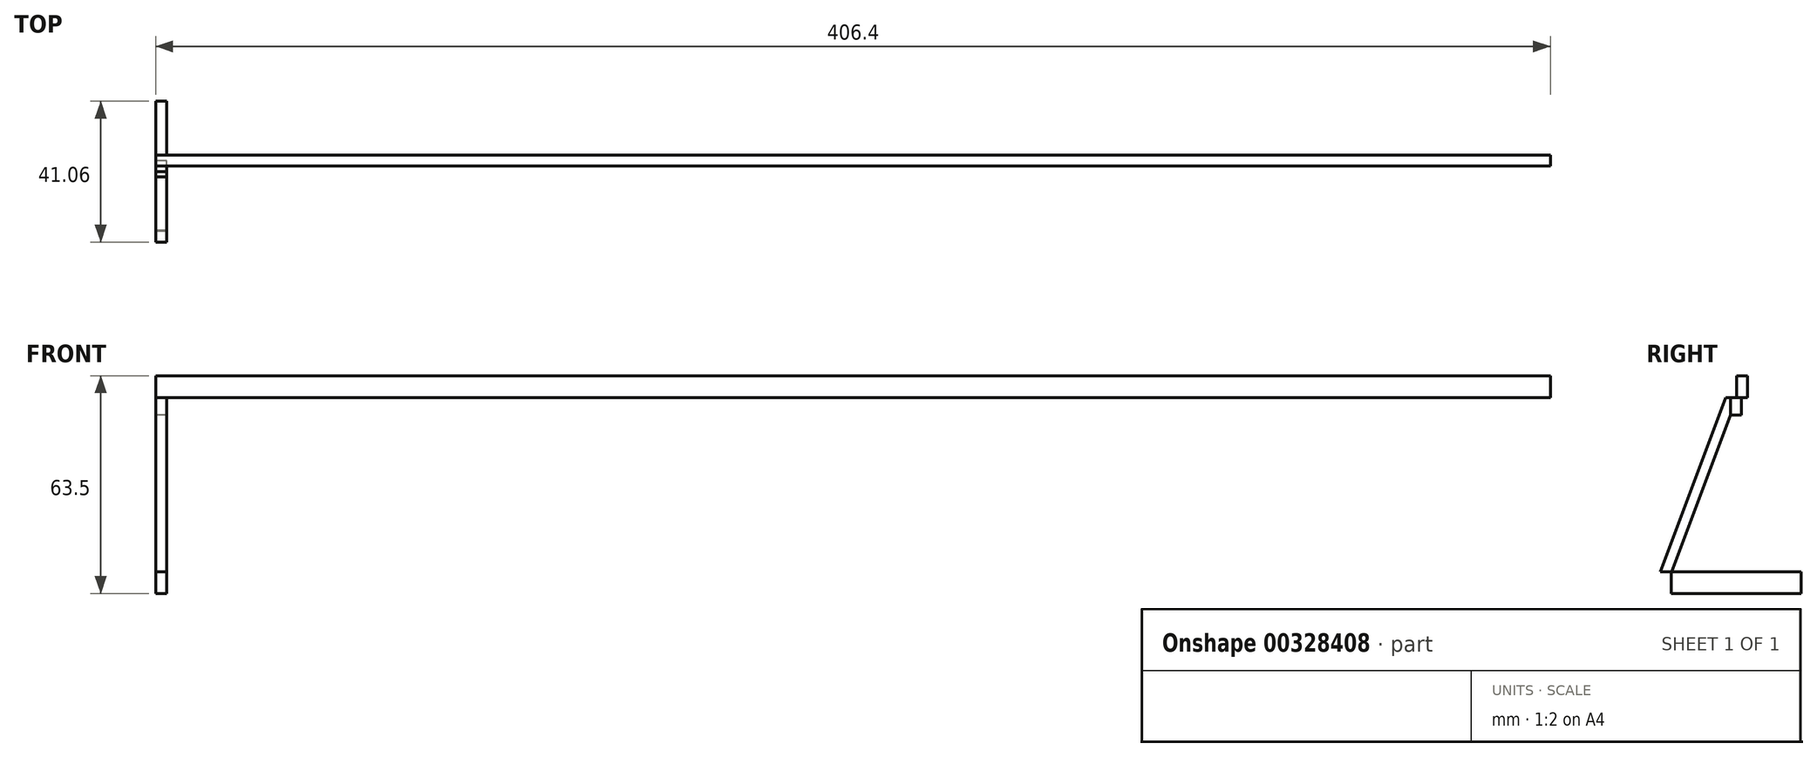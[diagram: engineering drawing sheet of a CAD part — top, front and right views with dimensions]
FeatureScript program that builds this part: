
annotation { "Feature Type Name" : "Feature", "Feature Type Description" : "" }
export const myFeature = defineFeature(function(context is Context, id is Id, definition is map)
    precondition{}
    {
        {
            var Q0;
            Q0=qCreatedBy(makeId("Right.planeOp"),FACE);
            var sketch = newSketch(context, id + "F0", { "sketchPlane" : qUnion([Q0])});
            skLineSegment(sketch, "E0", {"start": v(0, 0) * mm, "end": v(37.88, 0) * mm});
            skLineSegment(sketch, "E1", {"start": v(37.88, 0) * mm, "end": v(41.06, 0) * mm});
            skLineSegment(sketch, "E2", {"start": v(0, 0) * mm, "end": v(-3.17, 0) * mm});
            skLineSegment(sketch, "E3", {"start": v(41.06, 0) * mm, "end": v(41.06, 6.35) * mm});
            skLineSegment(sketch, "E4", {"start": v(-3.17, 0) * mm, "end": v(-3.17, 6.35) * mm});
            skLineSegment(sketch, "E5", {"start": v(0, 0) * mm, "end": v(0, 6.35) * mm});
            skLineSegment(sketch, "E6", {"start": v(37.88, 0) * mm, "end": v(37.88, 6.35) * mm});
            skLineSegment(sketch, "E7", {"start": v(-3.17, 6.35) * mm, "end": v(0, 6.35) * mm});
            skLineSegment(sketch, "E8", {"start": v(37.88, 6.35) * mm, "end": v(41.06, 6.35) * mm});
            skLineSegment(sketch, "E9", {"start": v(18.94, 0) * mm, "end": v(18.94, 52.05) * mm, "construction": true});
            skLineSegment(sketch, "E10", {"start": v(15.88, 57.15) * mm, "end": v(22.23, 57.15) * mm});
            skLineSegment(sketch, "E11", {"start": v(22.23, 57.15) * mm, "end": v(22.23, 63.5) * mm});
            skLineSegment(sketch, "E12", {"start": v(15.88, 57.15) * mm, "end": v(15.88, 63.5) * mm});
            skLineSegment(sketch, "E13", {"start": v(15.88, 63.5) * mm, "end": v(22.23, 63.5) * mm});
            skLineSegment(sketch, "E14", {"start": v(19.05, 57.15) * mm, "end": v(19.05, 63.5) * mm});
            skLineSegment(sketch, "E15", {"start": v(-3.17, 6.35) * mm, "end": v(15.88, 57.15) * mm});
            skLineSegment(sketch, "E16", {"start": v(22.23, 57.15) * mm, "end": v(41.06, 6.35) * mm});
            skLineSegment(sketch, "E17", {"start": v(0, 6.35) * mm, "end": v(37.88, 6.35) * mm});
            skLineSegment(sketch, "E18.trimOffspring", {"start": v(0.22, 6.35) * mm, "end": v(17.35, 52.05) * mm});
            skLineSegment(sketch, "E19", {"start": v(20.53, 52.05) * mm, "end": v(37.47, 6.35) * mm});
            skLineSegment(sketch, "E20", {"start": v(18.94, 6.35) * mm, "end": v(17.35, 6.35) * mm});
            skLineSegment(sketch, "E21", {"start": v(18.94, 6.35) * mm, "end": v(20.53, 6.35) * mm});
            skLineSegment(sketch, "E22", {"start": v(17.35, 6.35) * mm, "end": v(17.35, 52.05) * mm});
            skLineSegment(sketch, "E23", {"start": v(17.35, 52.05) * mm, "end": v(20.53, 52.05) * mm});
            skLineSegment(sketch, "E24", {"start": v(20.53, 52.05) * mm, "end": v(20.53, 6.35) * mm});
            skLineSegment(sketch, "E25", {"start": v(17.35, 52.05) * mm, "end": v(17.35, 57.15) * mm});
            skLineSegment(sketch, "E26", {"start": v(20.53, 52.05) * mm, "end": v(20.53, 57.15) * mm});
            skSolve(sketch);
        }
        {
            var Q0;
            {var subQ0=sQuery(id+"F0.wireOp",EDGE,"E11");Q0=makeQuery(id+"F0.imprint","IMPRINT",FACE,{"disambiguationData":[TD([[makeQuery(id+"F0.imprint","IMPRINT",EDGE,{"derivedFrom":subQ0}),1.0]])]});}
            extrude(context, id + "F1", {"entities" : qUnion([Q0]), "depth" : 406.4 * mm});
        }
        {
            var Q0;
            Q0=makeQuery(id+"F0.imprint","IMPRINT",FACE,{"disambiguationData":[TD([[makeQuery(id+"F0.imprint","IMPRINT",EDGE,{"derivedFrom":sQuery(id+"F0.wireOp",EDGE,"E7")}),1.0]])]});
            extrude(context, id + "F2", {"entities" : qUnion([Q0]), "depth" : 3.17 * mm});
        }
        {
            var Q0;
            Q0=makeQuery(id+"F0.imprint","IMPRINT",FACE,{"disambiguationData":[TD([[makeQuery(id+"F0.imprint","IMPRINT",EDGE,{"derivedFrom":sQuery(id+"F0.wireOp",EDGE,"E0")}),1.0]])]});
            extrude(context, id + "F3", {"entities" : qUnion([Q0]), "depth" : 3.17 * mm});
        }
        {
            var Q0;
            Q0=makeQuery(id+"F0.imprint","IMPRINT",FACE,{"disambiguationData":[TD([[makeQuery(id+"F0.imprint","IMPRINT",EDGE,{"derivedFrom":sQuery(id+"F0.wireOp",EDGE,"E20")}),-1.0]])]});
            var Q1;
            {var subQ0=sQuery(id+"F0.wireOp",EDGE,"pGliAPCi-6uMI-fG8I-oafq-WGV2nKLFa70K");Q1=makeQuery(id+"F0.imprint","IMPRINT",FACE,{"disambiguationData":[TD([[makeQuery(id+"F0.imprint","IMPRINT",EDGE,{"derivedFrom":subQ0}),1.0]])]});}
            var Q2;
            {var subQ3=sQuery(id+"F0.wireOp",EDGE,"E23");Q2=makeQuery(id+"F0.imprint","IMPRINT",FACE,{"disambiguationData":[TD([[makeQuery(id+"F0.imprint","IMPRINT",EDGE,{"derivedFrom":subQ3}),1.0]])]});}
            var Q3;
            {var subQ0=sQuery(id+"F0.wireOp",EDGE,"pGliAPCi-6uMI-fG8I-oafq-WGV2nKLFa70K");Q3=makeQuery(id+"F0.imprint","IMPRINT",FACE,{"disambiguationData":[TD([[makeQuery(id+"F0.imprint","IMPRINT",EDGE,{"derivedFrom":subQ0}),-1.0]])]});}
            extrude(context, id + "F4", {"entities" : qUnion([Q0, Q1, Q2, Q3]), "depth" : 3.17 * mm});
        }
    });
